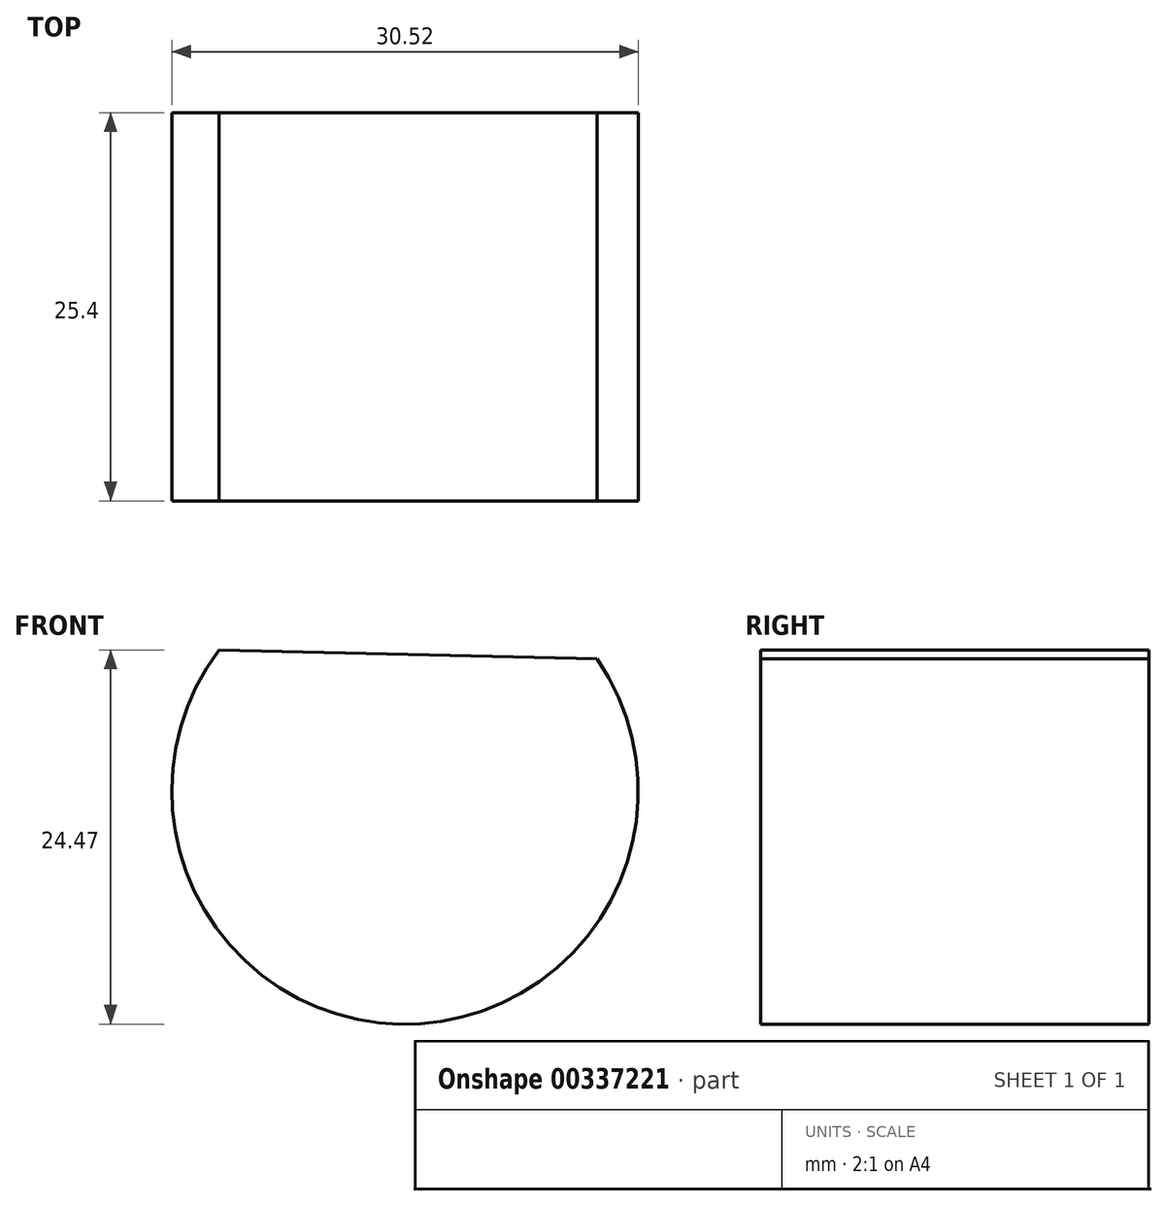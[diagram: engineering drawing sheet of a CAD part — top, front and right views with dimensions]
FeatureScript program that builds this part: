
annotation { "Feature Type Name" : "Feature", "Feature Type Description" : "" }
export const myFeature = defineFeature(function(context is Context, id is Id, definition is map)
    precondition{}
    {
        {
            var Q0;
            Q0=qCreatedBy(makeId("Front.planeOp"),FACE);
            var sketch = newSketch(context, id + "F0", { "sketchPlane" : qUnion([Q0])});
            skArc(sketch, "E0", {"start": v(-24.75, -28.5) * mm, "mid": v(-12.94, -52.96) * mm, "end": v(0, -29.07) * mm});
            skLineSegment(sketch, "E1", {"start": v(-24.75, -28.5) * mm, "end": v(-24.75, 28.78) * mm});
            skLineSegment(sketch, "E2", {"start": v(0, 29.64) * mm, "end": v(0, -29.07) * mm});
            skLineSegment(sketch, "E3", {"start": v(-24.75, 28.78) * mm, "end": v(0, 28.78) * mm});
            skLineSegment(sketch, "E4", {"start": v(-24.75, -28.5) * mm, "end": v(0, -29.07) * mm});
            skSolve(sketch);
        }
        {
            var Q0;
            Q0=makeQuery(id+"F0.imprint","IMPRINT",FACE,{"disambiguationData":[TD([[makeQuery(id+"F0.imprint","IMPRINT",EDGE,{"derivedFrom":sQuery(id+"F0.wireOp",EDGE,"E0")}),1.0]])]});
            extrude(context, id + "F1", {"entities" : qUnion([Q0]), "depth" : 25.4 * mm});
        }
    });
